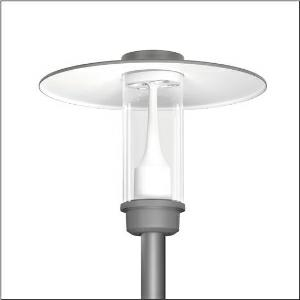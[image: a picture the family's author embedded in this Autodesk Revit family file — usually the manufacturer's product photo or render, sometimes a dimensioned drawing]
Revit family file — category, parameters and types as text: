
# Revit family: litepole_2_iq___p1_0a_5xa5425lf14hp_dc73
name_source: partatom
category: Lighting Fixtures
units: mm (PartAtom-declared; Revit-internal decimal feet)

## family parameters
Cut with Voids When Loaded = No
Host = Face
Light Source = No
Part Type = Normal
Room Calculation Point = No
Round Connector Dimension = Use Diameter
Shared = No

## types (1)
- --- (1 x LED, 4940 lm, 33.6 W, 4000K)
    Apparent Load = 34 VA
    CIE Flux Codes = 32 62 90 96 100
    Color Rendering = 70
    Color Temperature = 4000K
    Default Elevation = 1800 mm
    Description = Litepole 2 iQ, mast luminaire, Module 540 iQ-SR, primary light control with 3 zone facetted reflector, of plastic, silver coated, highly specular, structured, primary optical cover: cover, of PMMA, transparent, light distribution: P1.0a, light emission: direct distribution, primary light characteristic: strongly asymmetric, installation type: post-top, LED, High Power LED, rated luminous flux: 4.940lm, luminous efficacy: 147lm/W, light colour: 740, colour temperature: 4000K, control gear: iQ Street-Remote, control: pre-setting: logarithmic dimming characteristic, Street-Remote, Auto-Match, Temp-Guard, Lumen-Switch, Night-Set, Smart-Wire, Light-Fading, Desk-Remote (wireless, voltage-free reading and setting of iQ features in the workshop via application-optimized NFC function/RFID function), optimised constant luminous flux control (CLO 2.0), with terminal, 6-pole, max. 2.5mm², mains connection: 230..240V, AC, 50/60Hz, start of lifetime: 34W, end of service life: 36W, reduction: 15W, luminaire housing, upper part, of aluminium, coated, Siteco® metallic grey (DB 702S), diameter: 750mm, height: 590mm, spigot size: d x l = 76 x 70mm (post-top) | with reducer (optional accessory) 60 x 70mm, mounting height: 3..5m, post-top mast mounting element, of diecast aluminium, coated, Siteco® metallic grey (DB 702S), Module 540 iQ-SR, traffic white (RAL 9016), equipment: Power, protection rating (complete): IP65, insulation class (complete): insulation class II (safety insulation), certification: CE, ENEC, VDE, packaging unit: 1 piece

Light Distribution: P1.0a
    Height = 590 mm
    Lamp = 1 x LED
    Lamp Light Flux = 4940 lm
    Lamp Power = 33.6 W
    Lamp count = 1
    Length = 750 mm
    Luminous efficacy = 147 lm/W
    Manufacturer = Siteco
    ModVariant = No
    Model = 5XA5425LF14HP
    Number of Poles = 1
    OnlyDefault = Yes
    Power Factor = 1
    Product Name = Litepole 2 iQ | P1.0a
    Product group = mast luminaire | pylon top
    ProductGroupID = 6100
    Protection Class = Protection class II
    Protection Degree = IP 65
    RLX_Detail_Level = 1
    RLX_Emergency_Light_Flux = 0 lm
    RLX_Emergency_Type = 0
    RLX_Emergency_Type_DB = No
    RlxData = <blob elided: 32025 chars, md5=115d60ba>
    Socket = socket
    Standby Power = 0 W
    System Light Flux = 4940 lm
    System Power = 34 W
    Type Comments = factory setting: luminous flux: 100 % | dim-lin: 254 | 695 mA
    Type Image = l_1006518.jpg
    URL = http://relux.com
    VarID = @adj_189799
    Voltage = 0 V
    Weight = 0.00 kg
    Width = 0 mm  [stored 0 ft]

note: [stored X ft] marks values corroborated as IEEE doubles in the binary element streams (Revit-internal decimal feet)

## geometry (parser evidence)
native form markers: Blend x4, Sweep x9
no freeform markers — native parametric forms only
